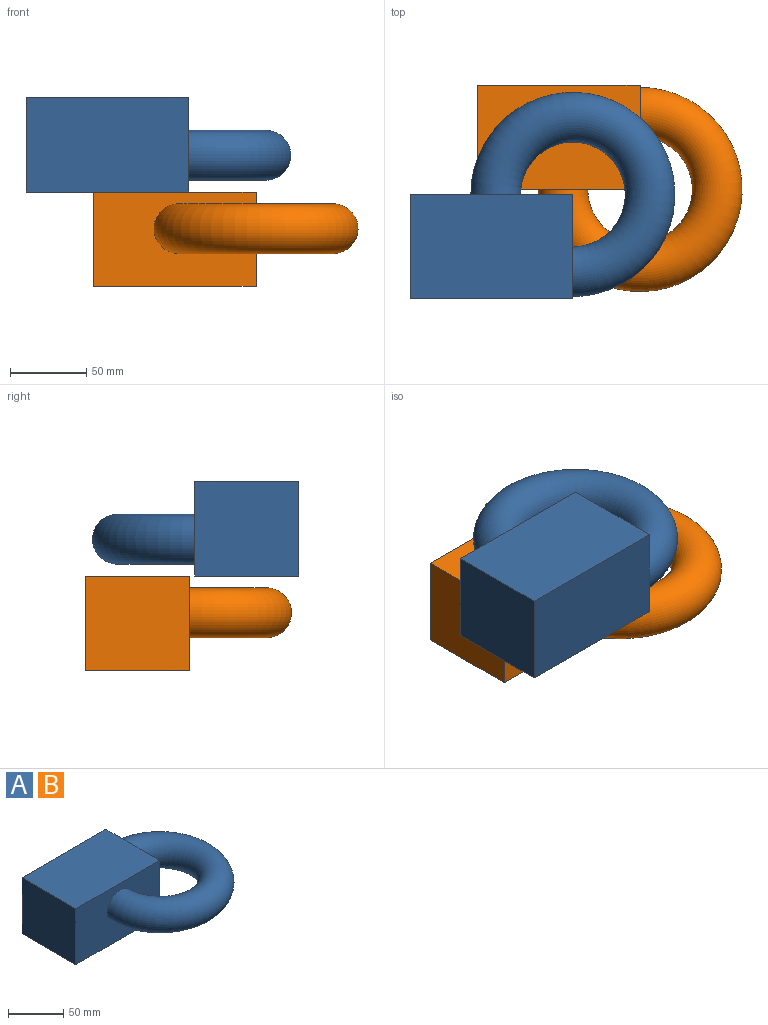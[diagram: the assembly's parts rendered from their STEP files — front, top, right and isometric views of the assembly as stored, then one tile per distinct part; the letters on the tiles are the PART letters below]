
ASSEMBLY  parts=2 mates=1
PART A: 7 faces, bbox 179.5x145.1x61.7 mm
  f0: plane 106.94x61.72mm, normal (0,1,0), area 6600.5mm2, adj f1,f3,f4,f5
  f1: plane 68.53x61.72mm, normal (-1,0,0), area 4230mm2, adj f0,f2,f4,f5
  f2: plane 106.94x61.72mm, normal (0,-1,0), area 5761.1mm2, adj f1,f3,f4,f5,f6
  f3: plane 68.53x61.72mm, normal (1,0,0), area 3390.6mm2, adj f0,f2,f4,f5,f6
  f4: plane 106.94x68.53mm, normal (0,0,1), area 7329mm2, adj f0,f1,f2,f3
  f5: plane 106.94x68.53mm, normal (0,0,-1), area 7329mm2, adj f0,f1,f2,f3
  f6: torus R=50.67mm, axis (0,0,1), area 24521.3mm2, adj f2,f3
PART B: same geometry as A
PLACE A rot(axis=(1,0,0),180deg) t=(-71.28,-16.89,62.33)mm
PLACE B t=(-27.17,26.56,-61.11)mm
MATE planar A.f4 <-> B.f4  axis (0,0,-1) through (-68.55,-31.08,0.61)mm
